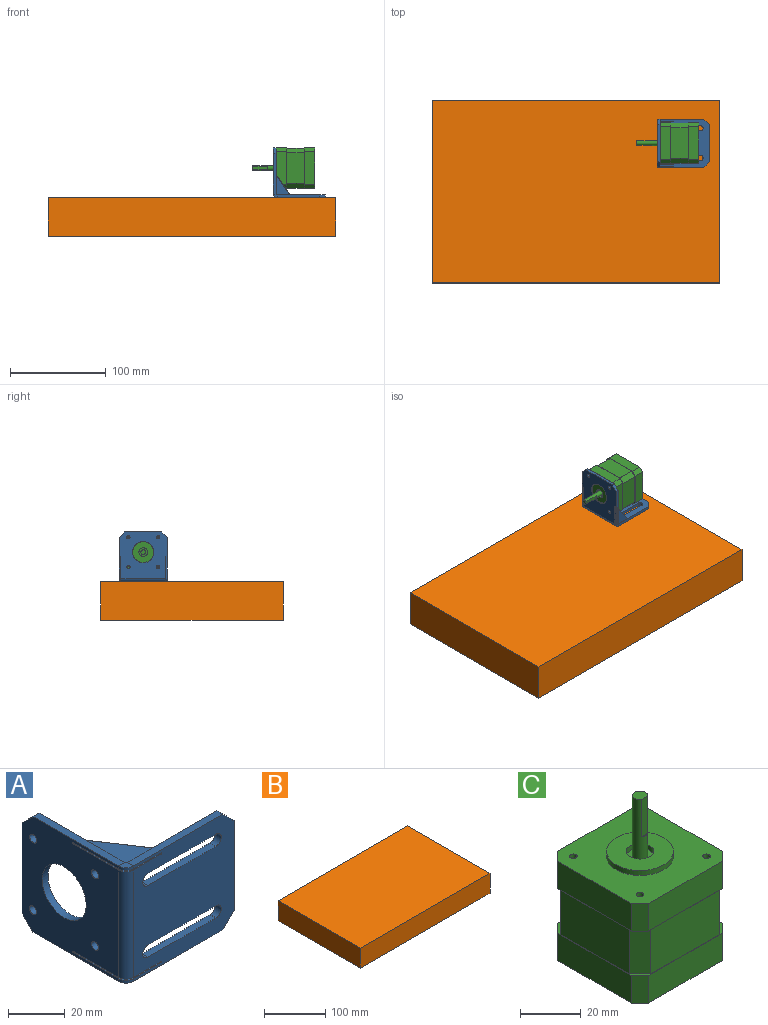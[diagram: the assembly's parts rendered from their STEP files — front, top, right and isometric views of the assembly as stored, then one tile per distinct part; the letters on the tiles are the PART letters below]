
ASSEMBLY  parts=3 mates=3
PART A: 53 faces, bbox 54.2x52.1x50 mm
  f0: plane 50.26x50mm, normal (0,-1,0), area 2064.4mm2, adj f2,f6,f9,f12,f13,f17,f23,f24
  f1: plane 50x48.26mm, normal (-1,0,0), area 1938.7mm2, adj f2,f6,f11,f13,f14,f16,f18,f19
  f2: cylinder r=3.74mm len=3.74mm, axis (0,0,1), area 7.3mm2, adj f0,f1,f8,f47
  f3: plane 50x48.26mm, normal (1,0,0), area 1860.3mm2, adj f5,f7,f11,f14,f15,f16,f18,f19
  f4: plane 50.26x50mm, normal (0,1,0), area 2012.1mm2, adj f5,f7,f9,f12,f15,f17,f23,f24
  f5: cylinder r=0.74mm len=0.74mm, axis (0,0,1), area 0.3mm2, adj f3,f4,f8,f45
  f6: cylinder r=3.74mm len=3.74mm, axis (0,0,1), area 7.3mm2, adj f0,f1,f10,f38
  f7: cylinder r=0.74mm len=0.74mm, axis (0,0,1), area 0.3mm2, adj f3,f4,f10,f36
  f8: plane 3.74x3.74mm, normal (0,0,-1), area 10.5mm2, adj f2,f5,f9,f16
  f9: plane 44.76x3mm, normal (0,0,-1), area 134.3mm2, adj f0,f4,f8,f32
  f10: plane 3.74x3.74mm, normal (0,0,1), area 10.5mm2, adj f6,f7,f11,f17
  f11: plane 42.76x3mm, normal (0,0,1), area 128.3mm2, adj f1,f3,f10,f34
  f12: plane 39x3mm, normal (1,0,0), area 117mm2, adj f0,f4,f32,f33
  f13: cylinder r=3.74mm len=46.5mm, axis (0,0,1), area 272.9mm2, adj f0,f1,f39,f48
  f14: plane 39x3mm, normal (0,1,0), area 117mm2, adj f1,f3,f31,f34
  f15: cylinder r=0.74mm len=44.5mm, axis (0,0,1), area 51.5mm2, adj f3,f4,f37,f46
  f16: plane 42.76x3mm, normal (0,0,-1), area 128.3mm2, adj f1,f3,f8,f31
  f17: plane 44.76x3mm, normal (0,0,1), area 134.3mm2, adj f0,f4,f10,f33
  f18: cylinder r=1.75mm len=3.5mm, axis (-1,0,0), area 33mm2, adj f1,f3
  f19: cylinder r=1.75mm len=3.5mm, axis (-1,0,0), area 33mm2, adj f1,f3
  f20: cylinder r=11.04mm len=22.08mm, axis (-1,0,0), area 208.1mm2, adj f1,f3
  f21: cylinder r=1.75mm len=3.5mm, axis (-1,0,0), area 33mm2, adj f1,f3
  f22: cylinder r=1.75mm len=3.5mm, axis (-1,0,0), area 33mm2, adj f1,f3
  f23: cylinder r=2.65mm len=5.3mm, axis (0,1,0), area 25mm2, adj f0,f4,f24,f26
  f24: plane 34x3mm, normal (0,0,-1), area 102mm2, adj f0,f4,f23,f25
  f25: cylinder r=2.65mm len=5.3mm, axis (0,1,0), area 25mm2, adj f0,f4,f24,f26
  f26: plane 34x3mm, normal (0,0,1), area 102mm2, adj f0,f4,f23,f25
  f27: cylinder r=2.65mm len=5.3mm, axis (0,1,0), area 25mm2, adj f0,f4,f28,f30
  f28: plane 34x3mm, normal (0,0,1), area 102mm2, adj f0,f4,f27,f29
  f29: cylinder r=2.65mm len=5.3mm, axis (0,1,0), area 25mm2, adj f0,f4,f28,f30
  f30: plane 34x3mm, normal (0,0,-1), area 102mm2, adj f0,f4,f27,f29
  f31: plane 5.5x5.5mm, normal (0,0.71,-0.71), area 23.3mm2, adj f1,f3,f14,f16
  f32: plane 5.5x5.5mm, normal (0.71,0,-0.71), area 23.3mm2, adj f0,f4,f9,f12
  f33: plane 5.5x5.5mm, normal (0.71,0,0.71), area 23.3mm2, adj f0,f4,f12,f17
  f34: plane 5.5x5.5mm, normal (0,0.71,0.71), area 23.3mm2, adj f1,f3,f11,f14
  f35: plane 21x14mm, normal (0.83,0.55,0), area 50.5mm2, adj f3,f4,f40,f41
  f36: plane 20.55x13.7mm, normal (0,0,1), area 140.6mm2, adj f3,f4,f7,f40
  f37: plane 20.55x13.7mm, normal (0,0,-1), area 140.6mm2, adj f3,f4,f15,f41
  f38: plane 26.25x17.5mm, normal (0,0,-1), area 226.6mm2, adj f0,f1,f6,f42
  f39: plane 26.25x17.5mm, normal (0,0,1), area 226.6mm2, adj f0,f1,f13,f43
  f40: cylinder r=0.25mm len=21.14mm, axis (-0.55,0.83,0), area 9.8mm2, adj f3,f4,f35,f36
  f41: cylinder r=0.25mm len=21.14mm, axis (0.55,-0.83,0), area 9.8mm2, adj f3,f4,f35,f37
  f42: cylinder r=0.25mm len=26.84mm, axis (0.55,-0.83,0), area 12.5mm2, adj f0,f1,f38,f43
  f43: cylinder r=0.25mm len=26.84mm, axis (-0.55,0.83,0), area 12.5mm2, adj f0,f1,f39,f42
  f44: plane 21x14mm, normal (0.83,0.55,0), area 50.5mm2, adj f3,f4,f49,f50
  f45: plane 20.55x13.7mm, normal (0,0,-1), area 140.6mm2, adj f3,f4,f5,f50
  f46: plane 20.55x13.7mm, normal (0,0,1), area 140.6mm2, adj f3,f4,f15,f49
  f47: plane 26.25x17.5mm, normal (0,0,1), area 226.6mm2, adj f0,f1,f2,f51
  f48: plane 26.25x17.5mm, normal (0,0,-1), area 226.6mm2, adj f0,f1,f13,f52
  f49: cylinder r=0.25mm len=21.14mm, axis (-0.55,0.83,0), area 9.8mm2, adj f3,f4,f44,f46
  f50: cylinder r=0.25mm len=21.14mm, axis (0.55,-0.83,0), area 9.8mm2, adj f3,f4,f44,f45
  f51: cylinder r=0.25mm len=26.84mm, axis (-0.55,0.83,0), area 12.5mm2, adj f0,f1,f47,f52
  f52: cylinder r=0.25mm len=26.84mm, axis (0.55,-0.83,0), area 12.5mm2, adj f0,f1,f48,f51
PART B: 6 faces, bbox 300x190x40 mm
  f0: plane 190x40mm, normal (-1,0,0), area 7600mm2, adj f1,f3,f4,f5
  f1: plane 300x40mm, normal (0,-1,0), area 12000mm2, adj f0,f2,f4,f5
  f2: plane 190x40mm, normal (1,0,0), area 7600mm2, adj f1,f3,f4,f5
  f3: plane 300x40mm, normal (0,1,0), area 12000mm2, adj f0,f2,f4,f5
  f4: plane 300x190mm, normal (0,0,1), area 57000mm2, adj f0,f1,f2,f3
  f5: plane 300x190mm, normal (0,0,-1), area 57000mm2, adj f0,f1,f2,f3
PART C: 62 faces, bbox 42.3x42.3x64.5 mm
  f0: plane 4x4mm, normal (0,0,-1), area 12.6mm2, adj f5
  f1: plane 4x4mm, normal (0,0,-1), area 12.6mm2, adj f6
  f2: plane 4x4mm, normal (0,0,-1), area 12.6mm2, adj f7
  f3: plane 4x4mm, normal (0,0,-1), area 12.6mm2, adj f8
  f4: plane 10x10mm, normal (0,0,-1), area 78.5mm2, adj f9
  f5: cylinder r=2mm len=4mm, axis (0,0,-1), area 25.1mm2, adj f0,f10
  f6: cylinder r=2mm len=4mm, axis (0,0,-1), area 25.1mm2, adj f1,f10
  f7: cylinder r=2mm len=4mm, axis (0,0,-1), area 25.1mm2, adj f2,f10
  f8: cylinder r=2mm len=4mm, axis (0,0,-1), area 25.1mm2, adj f3,f10
  f9: cylinder r=5mm len=10mm, axis (0,0,-1), area 62.8mm2, adj f4,f10
  f10: plane 42.3x42.3mm, normal (0,0,-1), area 1628.5mm2, adj f5,f6,f7,f8,f9,f14,f15,f16
  f11: plane 3x0.5mm, normal (0,0,1), area 1mm2, adj f12,f22
  f12: plane 15x3mm, normal (0,-1,0), area 45mm2, adj f11,f13,f22
  f13: plane 5x4.5mm, normal (0,0,1), area 18.6mm2, adj f12,f22
  f14: plane 34.3x11mm, normal (-1,0,0), area 377.3mm2, adj f10,f15,f21,f30
  f15: plane 11x4mm, normal (-0.71,0.71,0), area 62.2mm2, adj f10,f14,f16,f30
  f16: plane 34.3x11mm, normal (0,1,0), area 377.3mm2, adj f10,f15,f17,f30
  f17: plane 11x4mm, normal (0.71,0.71,0), area 62.2mm2, adj f10,f16,f18,f30
  f18: plane 34.3x11mm, normal (1,0,0), area 377.3mm2, adj f10,f17,f19,f30
  f19: plane 11x4mm, normal (0.71,-0.71,0), area 62.2mm2, adj f10,f18,f20,f30
  f20: plane 34.3x11mm, normal (0,-1,0), area 377.3mm2, adj f10,f19,f21,f30
  f21: plane 11x4mm, normal (-0.71,-0.71,0), area 62.2mm2, adj f10,f14,f20,f30
  f22: cylinder r=2.5mm len=24.5mm, axis (0,0,1), area 336.6mm2, adj f11,f12,f13,f32
  f23: cylinder r=0.2mm len=18mm, axis (0,0,-1), area 2.8mm2, adj f30,f33,f34,f42
  f24: cylinder r=0.2mm len=18mm, axis (0,0,1), area 2.8mm2, adj f30,f34,f35,f42
  f25: cylinder r=0.2mm len=18mm, axis (0,0,-1), area 2.8mm2, adj f30,f35,f36,f42
  f26: cylinder r=0.2mm len=18mm, axis (0,0,1), area 2.8mm2, adj f30,f36,f37,f42
  f27: cylinder r=0.2mm len=18mm, axis (0,0,-1), area 2.8mm2, adj f30,f37,f38,f42
  f28: cylinder r=0.2mm len=18mm, axis (0,0,1), area 2.8mm2, adj f30,f38,f39,f42
  f29: cylinder r=0.2mm len=18mm, axis (0,0,1), area 2.8mm2, adj f30,f33,f40,f42
  f30: plane 42.3x42.3mm, normal (0,0,1), area 51.7mm2, adj f14,f15,f16,f17,f18,f19,f20,f21
  f31: cylinder r=0.2mm len=18mm, axis (0,0,-1), area 2.8mm2, adj f30,f39,f40,f42
  f32: plane 9x9mm, normal (0,0,1), area 44mm2, adj f22,f41
  f33: plane 31.73x18mm, normal (1,0,0), area 571.2mm2, adj f23,f29,f30,f42
  f34: plane 18x4.88mm, normal (0.71,-0.71,0), area 124.3mm2, adj f23,f24,f30,f42
  f35: plane 31.73x18mm, normal (0,-1,0), area 571.2mm2, adj f24,f25,f30,f42
  f36: plane 18x4.88mm, normal (-0.71,-0.71,0), area 124.3mm2, adj f25,f26,f30,f42
  f37: plane 31.73x18mm, normal (-1,0,0), area 571.2mm2, adj f26,f27,f30,f42
  f38: plane 18x4.88mm, normal (-0.71,0.71,0), area 124.3mm2, adj f27,f28,f30,f42
  f39: plane 31.73x18mm, normal (0,1,0), area 571.2mm2, adj f28,f30,f31,f42
  f40: plane 18x4.88mm, normal (0.71,0.71,0), area 124.3mm2, adj f29,f30,f31,f42
  f41: cylinder r=4.5mm len=9mm, axis (0,0,1), area 56.5mm2, adj f32,f46
  f42: plane 42.3x42.3mm, normal (0,0,-1), area 51.7mm2, adj f23,f24,f25,f26,f27,f28,f29,f31
  f43: cone r=0mm half-angle=59deg, axis (0,0,1), area 5.7mm2, adj f55
  f44: cone r=0mm half-angle=59deg, axis (0,0,1), area 5.7mm2, adj f56
  f45: cone r=0mm half-angle=59deg, axis (0,0,1), area 5.7mm2, adj f57
  f46: plane 22x22mm, normal (0,0,1), area 316.5mm2, adj f41,f58
  f47: plane 11x4mm, normal (0.71,0.71,0), area 62.2mm2, adj f42,f48,f54,f60
  f48: plane 34.3x11mm, normal (0,1,0), area 377.3mm2, adj f42,f47,f49,f60
  f49: plane 11x4mm, normal (-0.71,0.71,0), area 62.2mm2, adj f42,f48,f50,f60
  f50: plane 34.3x11mm, normal (-1,0,0), area 377.3mm2, adj f42,f49,f51,f60
  f51: plane 11x4mm, normal (-0.71,-0.71,0), area 62.2mm2, adj f42,f50,f52,f60
  f52: plane 34.3x11mm, normal (0,-1,0), area 377.3mm2, adj f42,f51,f53,f60
  f53: plane 11x4mm, normal (0.71,-0.71,0), area 62.2mm2, adj f42,f52,f54,f60
  f54: plane 34.3x11mm, normal (1,0,0), area 377.3mm2, adj f42,f47,f53,f60
  f55: cylinder r=1.25mm len=7.5mm, axis (0,0,1), area 58.9mm2, adj f43,f60
  f56: cylinder r=1.25mm len=7.5mm, axis (0,0,1), area 58.9mm2, adj f44,f60
  f57: cylinder r=1.25mm len=7.5mm, axis (0,0,1), area 58.9mm2, adj f45,f60
  f58: cylinder r=11mm len=22mm, axis (0,0,1), area 138.2mm2, adj f46,f60
  f59: cone r=0mm half-angle=59deg, axis (0,0,1), area 5.7mm2, adj f61
  f60: plane 42.3x42.3mm, normal (0,0,1), area 1357.5mm2, adj f47,f48,f49,f50,f51,f52,f53,f54
  f61: cylinder r=1.25mm len=7.5mm, axis (0,0,1), area 58.9mm2, adj f59,f60
PLACE A rot(axis=(1,0,0),90deg) t=(233.73,123.58,37.7)mm
PLACE B t=(-1.27,2.67,-2.3)mm fixed
PLACE C rot(axis=(0,-1,0),90deg) t=(236.73,148.58,68.66)mm
MATE planar B.f4 <-> A.f0  axis (0,0,1) through (148.73,97.67,37.7)mm
MATE cylindrical A.f20 <-> C.f9  axis (-1,0,0) through (235.23,148.58,68.66)mm
MATE planar A.f3 <-> C.f60  axis (1,0,0) through (236.73,148.58,65.27)mm
